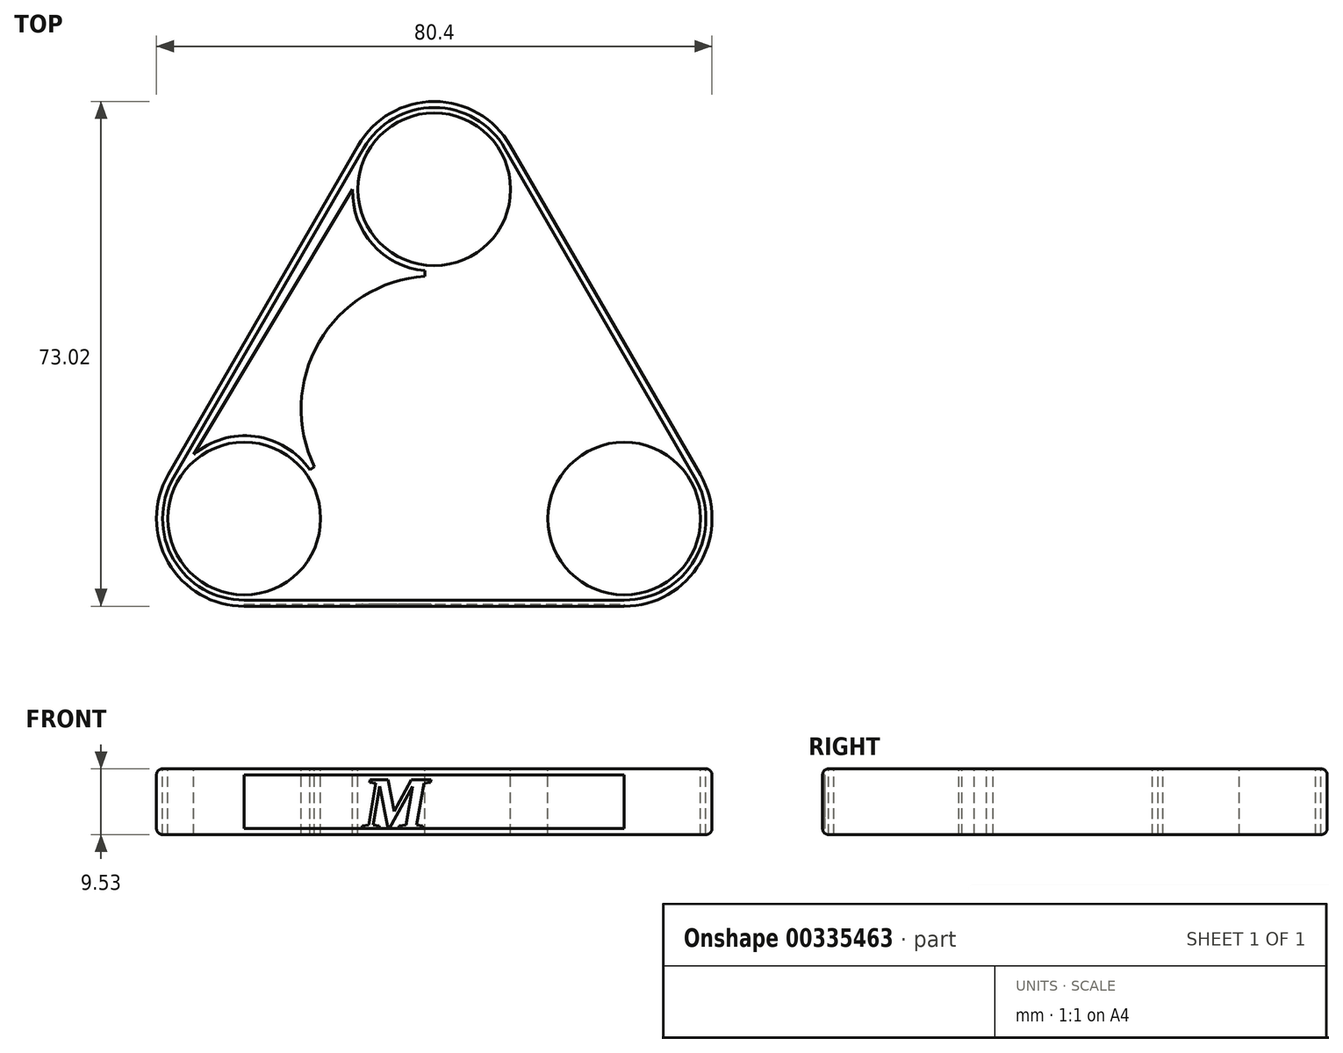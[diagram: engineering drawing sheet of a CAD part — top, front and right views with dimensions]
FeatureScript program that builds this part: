
annotation { "Feature Type Name" : "Feature", "Feature Type Description" : "" }
export const myFeature = defineFeature(function(context is Context, id is Id, definition is map)
    precondition{}
    {
        {
            var Q0;
            Q0=qCreatedBy(makeId("Top.planeOp"),FACE);
            var sketch = newSketch(context, id + "F0", { "sketchPlane" : qUnion([Q0])});
            skCircle(sketch, "E0", {"center": v(0, 0) * mm, "radius": 12.7 * mm});
            skCircle(sketch, "E1", {"center": v(0, 0) * mm, "radius": 11.05 * mm});
            skLineSegment(sketch, "E2", {"start": v(0, 0) * mm, "end": v(0, 31.75) * mm});
            skLineSegment(sketch, "E3", {"start": v(0, 0) * mm, "end": v(-27.5, -15.87) * mm});
            skLineSegment(sketch, "E4", {"start": v(0, 0) * mm, "end": v(27.5, -15.87) * mm});
            skCircle(sketch, "E5", {"center": v(0, 31.75) * mm, "radius": 12.7 * mm});
            skCircle(sketch, "E6", {"center": v(-27.5, -15.87) * mm, "radius": 12.7 * mm});
            skCircle(sketch, "E7", {"center": v(27.5, -15.87) * mm, "radius": 12.7 * mm});
            skCircle(sketch, "E8", {"center": v(-27.5, -15.87) * mm, "radius": 11.05 * mm});
            skCircle(sketch, "E9", {"center": v(27.5, -15.87) * mm, "radius": 11.05 * mm});
            skCircle(sketch, "E10", {"center": v(0, 31.75) * mm, "radius": 11.05 * mm});
            skLineSegment(sketch, "E11", {"start": v(-11, 38.1) * mm, "end": v(-38.5, -9.53) * mm});
            skLineSegment(sketch, "E12", {"start": v(38.5, -9.52) * mm, "end": v(11, 38.1) * mm});
            skLineSegment(sketch, "E13", {"start": v(-27.5, -28.57) * mm, "end": v(27.5, -28.57) * mm});
            skSolve(sketch);
        }
        {
            var Q0;
            Q0=makeQuery(id+"F0.imprint","IMPRINT",FACE,{"disambiguationData":[TD([[makeQuery(id+"F0.imprint","IMPRINT",EDGE,{"derivedFrom":sQuery(id+"F0.wireOp",EDGE,"E8")}),-1.0]])]});
            var Q1;
            Q1=makeQuery(id+"F0.imprint","IMPRINT",FACE,{"disambiguationData":[TD([[makeQuery(id+"F0.imprint","IMPRINT",EDGE,{"derivedFrom":sQuery(id+"F0.wireOp",EDGE,"E10")}),-1.0]])]});
            var Q2;
            Q2=makeQuery(id+"F0.imprint","IMPRINT",FACE,{"disambiguationData":[TD([[makeQuery(id+"F0.imprint","IMPRINT",EDGE,{"derivedFrom":sQuery(id+"F0.wireOp",EDGE,"E9")}),-1.0]])]});
            var Q3;
            {var subQ0=sQuery(id+"F0.wireOp",EDGE,"E2");var subQ1=sQuery(id+"F0.wireOp",EDGE,"E0");var subQ2=makeQuery(id+"F0.imprint","INTERSECT",VERTEX,{"derivedFrom":[subQ1,subQ0]});Q3=makeQuery(id+"F0.imprint","IMPRINT",FACE,{"disambiguationData":[TD([[makeQuery(id+"F0.imprint","IMPRINT",EDGE,{"disambiguationData":[TD([[subQ2,1.0]])],"derivedFrom":subQ1}),1.0]])]});}
            var Q4;
            {var subQ0=sQuery(id+"F0.wireOp",EDGE,"E3");var subQ1=sQuery(id+"F0.wireOp",EDGE,"E0");var subQ2=makeQuery(id+"F0.imprint","INTERSECT",VERTEX,{"derivedFrom":[subQ1,subQ0]});Q4=makeQuery(id+"F0.imprint","IMPRINT",FACE,{"disambiguationData":[TD([[makeQuery(id+"F0.imprint","IMPRINT",EDGE,{"disambiguationData":[TD([[subQ2,1.0]])],"derivedFrom":subQ1}),1.0]])]});}
            var Q5;
            {var subQ0=sQuery(id+"F0.wireOp",EDGE,"E3");var subQ1=sQuery(id+"F0.wireOp",EDGE,"E0");var subQ2=makeQuery(id+"F0.imprint","INTERSECT",VERTEX,{"derivedFrom":[subQ1,subQ0]});Q5=makeQuery(id+"F0.imprint","IMPRINT",FACE,{"disambiguationData":[TD([[makeQuery(id+"F0.imprint","IMPRINT",EDGE,{"disambiguationData":[TD([[subQ2,-1.0]])],"derivedFrom":subQ1}),1.0]])]});}
            var Q6;
            {var subQ0=sQuery(id+"F0.wireOp",EDGE,"E11");Q6=makeQuery(id+"F0.imprint","IMPRINT",FACE,{"disambiguationData":[TD([[makeQuery(id+"F0.imprint","IMPRINT",EDGE,{"derivedFrom":subQ0}),1.0]])]});}
            var Q7;
            {var subQ0=sQuery(id+"F0.wireOp",EDGE,"E13");Q7=makeQuery(id+"F0.imprint","IMPRINT",FACE,{"disambiguationData":[TD([[makeQuery(id+"F0.imprint","IMPRINT",EDGE,{"derivedFrom":subQ0}),1.0]])]});}
            var Q8;
            {var subQ9=sQuery(id+"F0.wireOp",EDGE,"E12");Q8=makeQuery(id+"F0.imprint","IMPRINT",FACE,{"disambiguationData":[TD([[makeQuery(id+"F0.imprint","IMPRINT",EDGE,{"derivedFrom":subQ9}),1.0]])]});}
            extrude(context, id + "F1", {"entities" : qUnion([Q0, Q1, Q2, Q3, Q4, Q5, Q6, Q7, Q8]), "depth" : 9.52 * mm, "offsetDistance" : 25.4 * mm});
        }
        {
            var Q0;
            Q0=makeQuery(id+"F1.opExtrude","CAP_FACE",FACE,{"disambiguationData":[OSD([sQuery(id+"F0.wireOp",EDGE,"E1"),sQuery(id+"F0.wireOp",EDGE,"E5"),sQuery(id+"F0.wireOp",EDGE,"E6"),sQuery(id+"F0.wireOp",EDGE,"E7"),sQuery(id+"F0.wireOp",EDGE,"E8"),sQuery(id+"F0.wireOp",EDGE,"E9"),sQuery(id+"F0.wireOp",EDGE,"E10"),sQuery(id+"F0.wireOp",EDGE,"E11"),sQuery(id+"F0.wireOp",EDGE,"E12"),sQuery(id+"F0.wireOp",EDGE,"E13")])],"isStart":false});
            var sketch = newSketch(context, id + "F2", { "sketchPlane" : qUnion([Q0])});
            skArc(sketch, "E14", {"start": v(-1.37, 15.8) * mm, "mid": v(-13.66, 7.89) * mm, "end": v(-14.37, -6.71) * mm});
            skArc(sketch, "E15", {"start": v(14.37, -6.71) * mm, "mid": v(13.66, 7.89) * mm, "end": v(1.37, 15.8) * mm});
            skArc(sketch, "E16", {"start": v(-13, -9.09) * mm, "mid": v(0, -15.78) * mm, "end": v(13, -9.09) * mm});
            skArc(sketch, "E17", {"start": v(-1.37, 17.83) * mm, "mid": v(-15.49, 8.94) * mm, "end": v(-16.13, -7.73) * mm});
            skLineSegment(sketch, "E18", {"start": v(-1.37, 20.79) * mm, "end": v(-1.37, 10.96) * mm});
            skLineSegment(sketch, "E19", {"start": v(1.37, 20.79) * mm, "end": v(1.37, 10.96) * mm});
            skPoint(sketch, "E20.trimOffspring.end.orphan", {"position": v(0, 20.7) * mm});
            skPoint(sketch, "E21.end.orphan", {"position": v(0, 15.88) * mm});
            skPoint(sketch, "E21.start.orphan", {"position": v(0, 11.05) * mm});
            skLineSegment(sketch, "E22.1.0", {"start": v(-17.32, -11.58) * mm, "end": v(-8.8, -6.67) * mm});
            skLineSegment(sketch, "E22.1.1", {"start": v(-18.69, -9.2) * mm, "end": v(-10.18, -4.3) * mm});
            skLineSegment(sketch, "E22.2.0", {"start": v(18.69, -9.2) * mm, "end": v(10.18, -4.3) * mm});
            skLineSegment(sketch, "E22.2.1", {"start": v(17.32, -11.58) * mm, "end": v(8.8, -6.67) * mm});
            skPoint(sketch, "E23.start.orphan", {"position": v(-9.57, -5.52) * mm});
            skPoint(sketch, "E24.trimOffspring.end.orphan", {"position": v(-17.93, -10.35) * mm});
            skArc(sketch, "E25.trimOffspring", {"start": v(-14.75, -10.1) * mm, "mid": v(0, -17.88) * mm, "end": v(14.75, -10.1) * mm});
            skPoint(sketch, "E26.orphan", {"position": v(-13.75, -7.94) * mm});
            skPoint(sketch, "E27.orphan", {"position": v(13.75, -7.94) * mm});
            skArc(sketch, "E28.trimOffspring", {"start": v(16.13, -7.73) * mm, "mid": v(15.49, 8.94) * mm, "end": v(1.37, 17.83) * mm});
            skPoint(sketch, "E29.orphan", {"position": v(17.93, -10.35) * mm});
            skPoint(sketch, "E30.start.orphan", {"position": v(9.57, -5.52) * mm});
            skSolve(sketch);
        }
        {
            var Q0;
            {var subQ0=sQuery(id+"F2.wireOp",EDGE,"E15");Q0=makeQuery(id+"F2.imprint","IMPRINT",FACE,{"disambiguationData":[TD([[makeQuery(id+"F2.imprint","IMPRINT",EDGE,{"derivedFrom":subQ0}),-1.0]])]});}
            var Q1;
            {var subQ0=sQuery(id+"F2.wireOp",EDGE,"E16");Q1=makeQuery(id+"F2.imprint","IMPRINT",FACE,{"disambiguationData":[TD([[makeQuery(id+"F2.imprint","IMPRINT",EDGE,{"derivedFrom":subQ0}),-1.0]])]});}
            var Q2;
            {var subQ0=sQuery(id+"F2.wireOp",EDGE,"E14");Q2=makeQuery(id+"F2.imprint","IMPRINT",FACE,{"disambiguationData":[TD([[makeQuery(id+"F2.imprint","IMPRINT",EDGE,{"derivedFrom":subQ0}),-1.0]])]});}
            extrude(context, id + "F3", {"entities" : qUnion([Q0, Q1, Q2]), "operationType" : NewBodyOperationType.REMOVE, "oppositeDirection" : true, "depth" : 25.4 * mm, "offsetDistance" : 25.4 * mm});
        }
        {
            var Q0;
            Q0=makeQuery(id+"F1.opExtrude","CAP_EDGE",EDGE,{"disambiguationData":[OSD([sQuery(id+"F0.wireOp",EDGE,"E11")])],"isStart":false});
            var Q1;
            Q1=makeQuery(id+"F1.opExtrude","SWEPT_FACE",FACE,{"disambiguationData":[OSD([sQuery(id+"F0.wireOp",EDGE,"E6")])]});
            var Q2;
            Q2=makeQuery(id+"F1.opExtrude","SWEPT_FACE",FACE,{"disambiguationData":[OSD([sQuery(id+"F0.wireOp",EDGE,"E13")])]});
            var Q3;
            Q3=makeQuery(id+"F1.opExtrude","SWEPT_FACE",FACE,{"disambiguationData":[OSD([sQuery(id+"F0.wireOp",EDGE,"E7")])]});
            var Q4;
            Q4=makeQuery(id+"F1.opExtrude","SWEPT_FACE",FACE,{"disambiguationData":[OSD([sQuery(id+"F0.wireOp",EDGE,"E12")])]});
            var Q5;
            Q5=makeQuery(id+"F1.opExtrude","SWEPT_FACE",FACE,{"disambiguationData":[OSD([sQuery(id+"F0.wireOp",EDGE,"E5")])]});
            fillet(context, id + "F4", {"entities" : qUnion([Q0, Q1, Q2, Q3, Q4, Q5]), "radius" : 0.89 * mm, "tangentPropagation" : true, "allowEdgeOverflow" : false});
        }
        {
            var Q0;
            Q0=makeQuery(id+"F1.opExtrude","SWEPT_FACE",FACE,{"disambiguationData":[OSD([sQuery(id+"F0.wireOp",EDGE,"E13")])]});
            var sketch = newSketch(context, id + "F5", { "sketchPlane" : qUnion([Q0])});
            skText(sketch, "E31", { "text": "FMHS", "fontName": "Tinos-BoldItalic.ttf"});
            const initialGuessF5  = {"E31": [-0.01754, 0.00089, 1, 0, 0.00775]};
            skSetInitialGuess(sketch, initialGuessF5);
            skSolve(sketch);
        }
        {
            var Q0;
            Q0=makeQuery(id+"F5.imprint","IMPRINT",FACE,{"disambiguationData":[TD([[makeQuery(id+"F5.imprint","IMPRINT",EDGE,{"derivedFrom":sQuery(id+"F5.wireOp",EDGE,"E31.sketch_text.stroke-0")}),-1.0]])]});
            var Q1;
            Q1=makeQuery(id+"F5.imprint","IMPRINT",FACE,{"disambiguationData":[TD([[makeQuery(id+"F5.imprint","IMPRINT",EDGE,{"derivedFrom":sQuery(id+"F5.wireOp",EDGE,"E31.sketch_text.stroke-24")}),1.0]])]});
            var Q2;
            Q2=makeQuery(id+"F5.imprint","IMPRINT",FACE,{"disambiguationData":[TD([[makeQuery(id+"F5.imprint","IMPRINT",EDGE,{"derivedFrom":sQuery(id+"F5.wireOp",EDGE,"E31.sketch_text.stroke-49")}),-1.0]])]});
            var Q3;
            {var subQ0=sQuery(id+"F5.wireOp",EDGE,"E31.sketch_text.stroke-78");Q3=makeQuery(id+"F5.imprint","IMPRINT",FACE,{"disambiguationData":[TD([[makeQuery(id+"F5.imprint","IMPRINT",EDGE,{"derivedFrom":subQ0}),-1.0]])]});}
            extrude(context, id + "F6", {"entities" : qUnion([Q0, Q1, Q2, Q3]), "operationType" : NewBodyOperationType.REMOVE, "oppositeDirection" : true, "depth" : 0.3 * mm, "offsetDistance" : 25.4 * mm});
        }
        {
            var Q0;
            Q0=makeQuery(id+"F1.opExtrude","CAP_FACE",FACE,{"disambiguationData":[OSD([sQuery(id+"F0.wireOp",EDGE,"E1"),sQuery(id+"F0.wireOp",EDGE,"E5"),sQuery(id+"F0.wireOp",EDGE,"E6"),sQuery(id+"F0.wireOp",EDGE,"E7"),sQuery(id+"F0.wireOp",EDGE,"E8"),sQuery(id+"F0.wireOp",EDGE,"E9"),sQuery(id+"F0.wireOp",EDGE,"E10"),sQuery(id+"F0.wireOp",EDGE,"E11"),sQuery(id+"F0.wireOp",EDGE,"E12"),sQuery(id+"F0.wireOp",EDGE,"E13")])],"isStart":false});
            var sketch = newSketch(context, id + "F7", { "sketchPlane" : qUnion([Q0])});
            skLineSegment(sketch, "E32", {"start": v(-1.37, 19.17) * mm, "end": v(-1.37, 19.17) * mm});
            skLineSegment(sketch, "E33", {"start": v(-17.28, -8.4) * mm, "end": v(-17.32, -8.42) * mm});
            skLineSegment(sketch, "E34", {"start": v(17.32, -8.42) * mm, "end": v(18, -8.81) * mm});
            skLineSegment(sketch, "E35", {"start": v(15.95, -10.8) * mm, "end": v(16.63, -11.19) * mm});
            skArc(sketch, "E36", {"start": v(-1.37, 17.83) * mm, "mid": v(-15.48, 8.93) * mm, "end": v(-16.13, -7.73) * mm});
            skArc(sketch, "E37", {"start": v(16.13, -7.73) * mm, "mid": v(15.47, 8.93) * mm, "end": v(1.37, 17.83) * mm});
            skArc(sketch, "E38", {"start": v(-14.75, -10.1) * mm, "mid": v(0, -17.86) * mm, "end": v(14.75, -10.1) * mm});
            skLineSegment(sketch, "E39", {"start": v(-15.92, -10.77) * mm, "end": v(-16.62, -11.18) * mm});
            skArc(sketch, "E40", {"start": v(-15.92, -10.77) * mm, "mid": v(0.01, -19.25) * mm, "end": v(15.95, -10.8) * mm});
            skArc(sketch, "E41.trimOffspring", {"start": v(17.32, -8.42) * mm, "mid": v(16.67, 9.61) * mm, "end": v(1.37, 19.17) * mm});
            skArc(sketch, "E42", {"start": v(1.37, 19.98) * mm, "mid": v(8.92, 23.8) * mm, "end": v(11.81, 31.75) * mm});
            skPoint(sketch, "E43.orphan", {"position": v(1.37, 20.79) * mm});
            skLineSegment(sketch, "E44", {"start": v(1.37, 19.17) * mm, "end": v(1.37, 19.98) * mm});
            skLineSegment(sketch, "E45", {"start": v(11.81, 31.75) * mm, "end": v(34.83, -6.62) * mm});
            skArc(sketch, "E46", {"start": v(34.83, -6.62) * mm, "mid": v(25.93, -4) * mm, "end": v(18, -8.81) * mm});
            skPoint(sketch, "E47.orphan", {"position": v(18.69, -9.2) * mm});
            skLineSegment(sketch, "E48", {"start": v(11.81, 31.75) * mm, "end": v(11.05, 31.75) * mm});
            skArc(sketch, "E49.MirrorCS", {"start": v(-1.37, 19.98) * mm, "mid": v(-8.92, 23.8) * mm, "end": v(-11.81, 31.75) * mm});
            skArc(sketch, "E50.MirrorCS", {"start": v(-17.32, -8.42) * mm, "mid": v(-16.67, 9.61) * mm, "end": v(-1.37, 19.17) * mm});
            skArc(sketch, "E51.MirrorCS", {"start": v(-34.83, -6.62) * mm, "mid": v(-25.93, -4) * mm, "end": v(-18, -8.81) * mm});
            skLineSegment(sketch, "E52.MirrorCS", {"start": v(-11.81, 31.75) * mm, "end": v(-34.83, -6.62) * mm});
            skPoint(sketch, "E53.MirrorCS.end.orphan", {"position": v(-1.37, 19.98) * mm});
            skLineSegment(sketch, "E54", {"start": v(-17.32, -8.42) * mm, "end": v(-18, -8.81) * mm});
            skLineSegment(sketch, "E55", {"start": v(-1.37, 19.17) * mm, "end": v(-1.37, 19.98) * mm});
            skArc(sketch, "E56", {"start": v(-19.59, -24.65) * mm, "mid": v(-15.85, -18.4) * mm, "end": v(-16.62, -11.18) * mm});
            skPoint(sketch, "E57.orphan", {"position": v(-17.32, -11.58) * mm});
            skArc(sketch, "E58", {"start": v(16.63, -11.19) * mm, "mid": v(15.87, -18.4) * mm, "end": v(19.59, -24.65) * mm});
            skPoint(sketch, "E59.orphan", {"position": v(17.32, -11.58) * mm});
            skLineSegment(sketch, "E60", {"start": v(-19.59, -24.65) * mm, "end": v(19.59, -24.65) * mm});
            skSolve(sketch);
        }
        {
            var Q0;
            Q0=makeQuery(id+"F7.imprint","IMPRINT",FACE,{"disambiguationData":[TD([[makeQuery(id+"F7.imprint","IMPRINT",EDGE,{"derivedFrom":sQuery(id+"F7.wireOp",EDGE,"E34")}),1.0]])]});
            var Q1;
            Q1=makeQuery(id+"F7.imprint","IMPRINT",FACE,{"disambiguationData":[TD([[makeQuery(id+"F7.imprint","IMPRINT",EDGE,{"derivedFrom":sQuery(id+"F7.wireOp",EDGE,"E49.MirrorCS")}),1.0]])]});
            extrude(context, id + "F8", {"entities" : qUnion([Q0, Q1]), "operationType" : NewBodyOperationType.REMOVE, "oppositeDirection" : true, "depth" : 25.4 * mm, "offsetDistance" : 25.4 * mm});
        }
        {
            var Q0;
            Q0=makeQuery(id+"F7.imprint","IMPRINT",FACE,{"disambiguationData":[TD([[makeQuery(id+"F7.imprint","IMPRINT",EDGE,{"derivedFrom":sQuery(id+"F7.wireOp",EDGE,"E35")}),-1.0]])]});
            extrude(context, id + "F9", {"entities" : qUnion([Q0]), "operationType" : NewBodyOperationType.REMOVE, "oppositeDirection" : true, "depth" : 25.4 * mm});
        }
        {
            var Q0;
            Q0=makeQuery(id+"F1.opExtrude","CAP_FACE",FACE,{"disambiguationData":[OSD([sQuery(id+"F0.wireOp",EDGE,"E1"),sQuery(id+"F0.wireOp",EDGE,"E5"),sQuery(id+"F0.wireOp",EDGE,"E6"),sQuery(id+"F0.wireOp",EDGE,"E7"),sQuery(id+"F0.wireOp",EDGE,"E8"),sQuery(id+"F0.wireOp",EDGE,"E9"),sQuery(id+"F0.wireOp",EDGE,"E10"),sQuery(id+"F0.wireOp",EDGE,"E11"),sQuery(id+"F0.wireOp",EDGE,"E12"),sQuery(id+"F0.wireOp",EDGE,"E13")])],"isStart":false});
            var sketch = newSketch(context, id + "F10", { "sketchPlane" : qUnion([Q0])});
            skCircle(sketch, "E61", {"center": v(-27.5, -15.87) * mm, "radius": 11.05 * mm});
            skCircle(sketch, "E62", {"center": v(27.5, -15.87) * mm, "radius": 11.05 * mm});
            skCircle(sketch, "E63", {"center": v(0, 31.75) * mm, "radius": 11.05 * mm});
            skSolve(sketch);
        }
        {
            var Q0;
            Q0=makeQuery(id+"F10.imprint","IMPRINT",FACE,{"disambiguationData":[TD([[makeQuery(id+"F10.imprint","IMPRINT",EDGE,{"derivedFrom":sQuery(id+"F10.wireOp",EDGE,"E63")}),1.0]])]});
            var Q1;
            Q1=makeQuery(id+"F10.imprint","IMPRINT",FACE,{"disambiguationData":[TD([[makeQuery(id+"F10.imprint","IMPRINT",EDGE,{"derivedFrom":sQuery(id+"F10.wireOp",EDGE,"E62")}),1.0]])]});
            var Q2;
            Q2=makeQuery(id+"F10.imprint","IMPRINT",FACE,{"disambiguationData":[TD([[makeQuery(id+"F10.imprint","IMPRINT",EDGE,{"derivedFrom":sQuery(id+"F10.wireOp",EDGE,"E61")}),1.0]])]});
            extrude(context, id + "F11", {"entities" : qUnion([Q0, Q1, Q2]), "operationType" : NewBodyOperationType.ADD, "oppositeDirection" : true, "depth" : 9.52 * mm});
        }
    });
